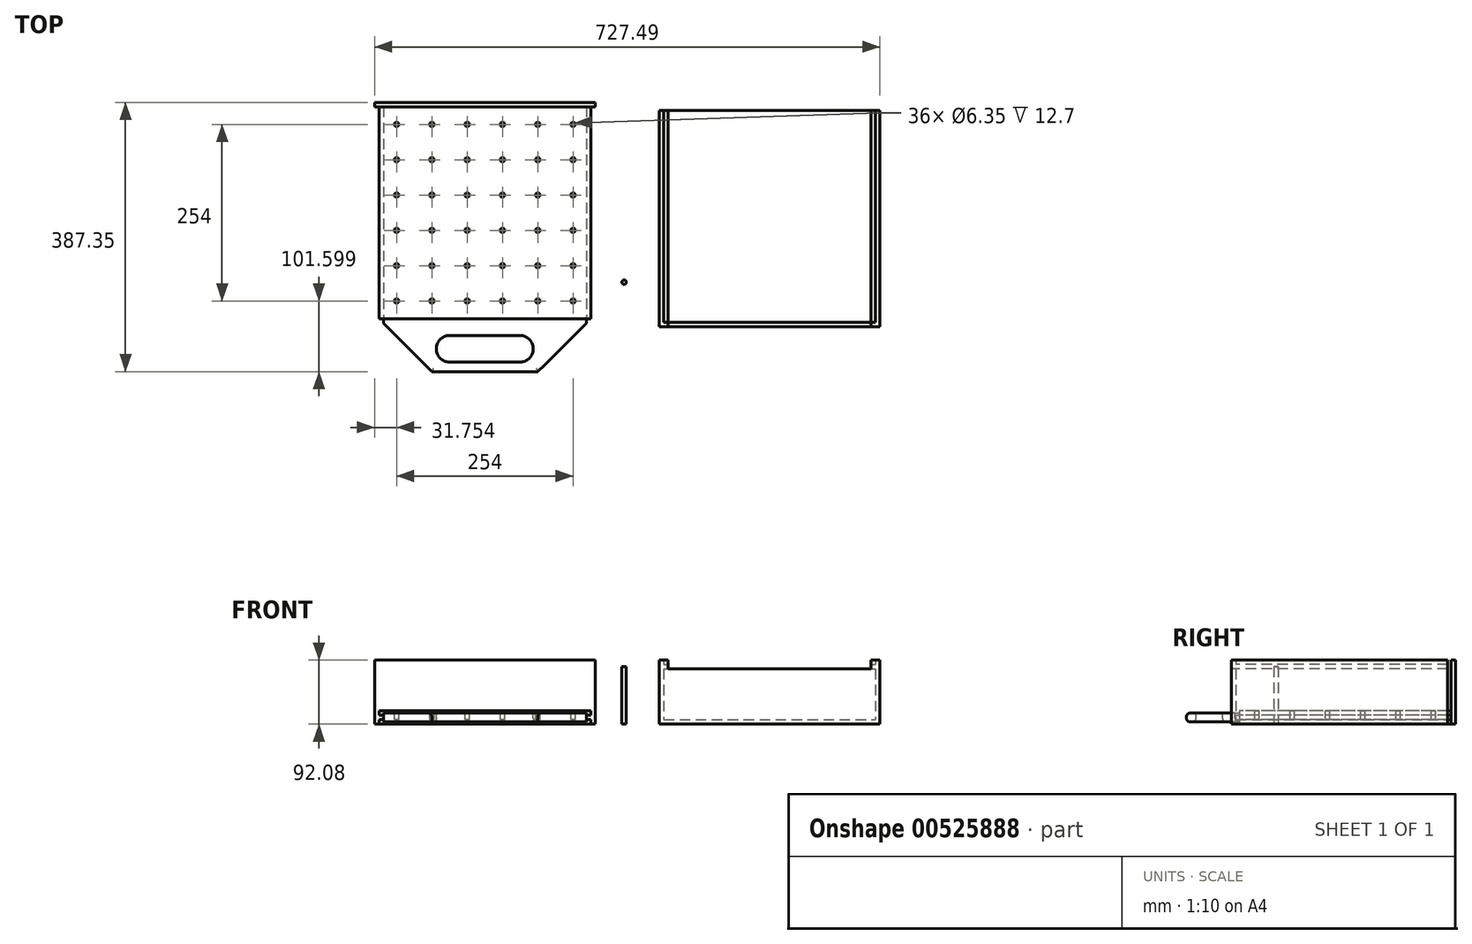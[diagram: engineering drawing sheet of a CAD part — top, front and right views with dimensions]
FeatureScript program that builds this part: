
annotation { "Feature Type Name" : "Feature", "Feature Type Description" : "" }
export const myFeature = defineFeature(function(context is Context, id is Id, definition is map)
    precondition{}
    {
        {
            var Q0;
            Q0=qCreatedBy(makeId("Top.planeOp"),FACE);
            var sketch = newSketch(context, id + "F0", { "sketchPlane" : qUnion([Q0])});
            skLineSegment(sketch, "E0.bottom", {"start": v(-147.49, 152.37) * mm, "end": v(157.31, 152.37) * mm});
            skLineSegment(sketch, "E0.top", {"start": v(-147.49, -152.43) * mm, "end": v(157.31, -152.43) * mm});
            skLineSegment(sketch, "E0.left", {"start": v(-147.49, 152.37) * mm, "end": v(-147.49, -152.43) * mm});
            skLineSegment(sketch, "E0.right", {"start": v(157.31, 152.37) * mm, "end": v(157.31, -152.43) * mm});
            skSolve(sketch);
        }
        {
            var Q0;
            Q0 = qSketchRegion(id + "F0", true);
            extrude(context, id + "F1", {"entities" : qUnion([Q0]), "depth" : 19.05 * mm, "offsetDistance" : 25.4 * mm});
        }
        {
            var Q0;
            Q0=makeQuery(id+"F1.opExtrude","SWEPT_FACE",FACE,{"disambiguationData":[OSD([sQuery(id+"F0.wireOp",EDGE,"E0.top")])]});
            var sketch = newSketch(context, id + "F2", { "sketchPlane" : qUnion([Q0])});
            skLineSegment(sketch, "E1.bottom", {"start": v(-147.49, 12.7) * mm, "end": v(-141.14, 12.7) * mm});
            skLineSegment(sketch, "E1.top", {"start": v(-147.49, 6.35) * mm, "end": v(-141.14, 6.35) * mm});
            skLineSegment(sketch, "E1.left", {"start": v(-147.49, 12.7) * mm, "end": v(-147.49, 6.35) * mm});
            skLineSegment(sketch, "E1.right", {"start": v(-141.14, 12.7) * mm, "end": v(-141.14, 6.35) * mm});
            skLineSegment(sketch, "E2.bottom", {"start": v(150.96, 12.7) * mm, "end": v(157.31, 12.7) * mm});
            skLineSegment(sketch, "E2.top", {"start": v(150.96, 6.35) * mm, "end": v(157.31, 6.35) * mm});
            skLineSegment(sketch, "E2.left", {"start": v(150.96, 12.7) * mm, "end": v(150.96, 6.35) * mm});
            skLineSegment(sketch, "E2.right", {"start": v(157.31, 12.7) * mm, "end": v(157.31, 6.35) * mm});
            skLineSegment(sketch, "E3.bottom", {"start": v(-141.24, 15.88) * mm, "end": v(150.86, 15.88) * mm});
            skLineSegment(sketch, "E3.top", {"start": v(-141.24, 3.18) * mm, "end": v(150.86, 3.18) * mm});
            skLineSegment(sketch, "E3.left", {"start": v(-141.24, 15.88) * mm, "end": v(-141.24, 3.18) * mm});
            skLineSegment(sketch, "E3.right", {"start": v(150.86, 15.88) * mm, "end": v(150.86, 3.18) * mm});
            skSolve(sketch);
        }
        {
            var Q0;
            Q0=makeQuery(id+"F2.imprint","IMPRINT",FACE,{"disambiguationData":[TD([[makeQuery(id+"F2.imprint","IMPRINT",EDGE,{"derivedFrom":sQuery(id+"F2.wireOp",EDGE,"E2.bottom")}),-1.0]])]});
            var Q1;
            {var subQ0=sQuery(id+"F2.wireOp",EDGE,"E1.left");Q1=makeQuery(id+"F2.imprint","IMPRINT",FACE,{"disambiguationData":[TD([[makeQuery(id+"F2.imprint","IMPRINT",EDGE,{"derivedFrom":subQ0}),1.0]])]});}
            extrude(context, id + "F3", {"entities" : qUnion([Q0, Q1]), "operationType" : NewBodyOperationType.REMOVE, "endBound" : BoundingType.THROUGH_ALL, "oppositeDirection" : true, "depth" : 25.4 * mm, "offsetDistance" : 25.4 * mm});
        }
        {
            var Q0;
            {var subQ1=sQuery(id+"F2.wireOp",EDGE,"E1.right");Q0=makeQuery(id+"F2.imprint","IMPRINT",FACE,{"disambiguationData":[TD([[makeQuery(id+"F2.imprint","IMPRINT",EDGE,{"derivedFrom":subQ1}),1.0]])]});}
            extrude(context, id + "F4", {"entities" : qUnion([Q0]), "operationType" : NewBodyOperationType.ADD, "depth" : 76.2 * mm, "offsetDistance" : 25.4 * mm});
        }
        {
            var Q0;
            Q0=makeQuery(id+"F4.opExtrude","SWEPT_FACE",FACE,{"disambiguationData":[OSD([sQuery(id+"F2.wireOp",EDGE,"E3.bottom")])]});
            var sketch = newSketch(context, id + "F5", { "sketchPlane" : qUnion([Q0])});
            skLineSegment(sketch, "E4", {"start": v(-141.24, -158.78) * mm, "end": v(150.86, -158.78) * mm, "construction": true});
            skLineSegment(sketch, "E5", {"start": v(-141.24, -158.78) * mm, "end": v(-71.39, -228.63) * mm});
            skLineSegment(sketch, "E6", {"start": v(150.86, -158.78) * mm, "end": v(81.01, -228.63) * mm});
            skLineSegment(sketch, "E7", {"start": v(-45.99, -195.8) * mm, "end": v(55.61, -195.8) * mm});
            skArc(sketch, "E8.0.startCap", {"start": v(-45.99, -214.85) * mm, "mid": v(-65.04, -195.8) * mm, "end": v(-45.99, -176.75) * mm});
            skArc(sketch, "E8.0.endCap", {"start": v(55.61, -176.75) * mm, "mid": v(74.66, -195.8) * mm, "end": v(55.61, -214.85) * mm});
            skLineSegment(sketch, "E8.0.left", {"start": v(-45.99, -176.75) * mm, "end": v(55.61, -176.75) * mm});
            skLineSegment(sketch, "E8.0.right", {"start": v(-45.99, -214.85) * mm, "end": v(55.61, -214.85) * mm});
            skSolve(sketch);
        }
        {
            var Q0;
            Q0 = qSketchRegion(id + "F5", true);
            var Q1;
            {var subQ0=sQuery(id+"F5.wireOp",EDGE,"E6");Q1=makeQuery(id+"F5.imprint","IMPRINT",FACE,{"disambiguationData":[TD([[makeQuery(id+"F5.imprint","IMPRINT",EDGE,{"derivedFrom":subQ0}),1.0]])]});}
            var Q2;
            {var subQ0=sQuery(id+"F5.wireOp",EDGE,"E5");Q2=makeQuery(id+"F5.imprint","IMPRINT",FACE,{"disambiguationData":[TD([[makeQuery(id+"F5.imprint","IMPRINT",EDGE,{"derivedFrom":subQ0}),-1.0]])]});}
            extrude(context, id + "F6", {"entities" : qUnion([Q0, Q1, Q2]), "operationType" : NewBodyOperationType.REMOVE, "oppositeDirection" : true, "depth" : 25.4 * mm, "offsetDistance" : 25.4 * mm});
        }
        {
            var Q0;
            Q0=makeQuery(id+"F6.boolean.opBoolean","COPY",EDGE,{"derivedFrom":makeQuery(id+"F6.opExtrude","CAP_EDGE",EDGE,{"disambiguationData":[OSD([sQuery(id+"F5.wireOp",EDGE,"E8.0.startCap")])],"isStart":true})});
            var Q1;
            Q1=makeQuery(id+"F6.boolean.opBoolean","COPY",EDGE,{"derivedFrom":makeQuery(id+"F6.opExtrude","CAP_EDGE",EDGE,{"disambiguationData":[OSD([sQuery(id+"F5.wireOp",EDGE,"E8.0.left")])],"isStart":true})});
            var Q2;
            Q2=makeQuery(id+"F6.boolean.opBoolean","INTERSECT",EDGE,{"derivedFrom":[makeQuery(id+"F4.opExtrude","SWEPT_FACE",FACE,{"disambiguationData":[OSD([sQuery(id+"F2.wireOp",EDGE,"E3.top")])]}),makeQuery(id+"F6.opExtrude","SWEPT_FACE",FACE,{"disambiguationData":[OSD([sQuery(id+"F5.wireOp",EDGE,"E8.0.left")])]})]});
            var Q3;
            Q3=makeQuery(id+"F6.boolean.opBoolean","INTERSECT",EDGE,{"derivedFrom":[makeQuery(id+"F4.opExtrude","SWEPT_FACE",FACE,{"disambiguationData":[OSD([sQuery(id+"F2.wireOp",EDGE,"E3.top")])]}),makeQuery(id+"F6.opExtrude","SWEPT_FACE",FACE,{"disambiguationData":[OSD([sQuery(id+"F5.wireOp",EDGE,"E8.0.startCap")])]})]});
            var Q4;
            Q4=makeQuery(id+"F6.boolean.opBoolean","INTERSECT",EDGE,{"derivedFrom":[makeQuery(id+"F4.opExtrude","SWEPT_FACE",FACE,{"disambiguationData":[OSD([sQuery(id+"F2.wireOp",EDGE,"E3.top")])]}),makeQuery(id+"F6.opExtrude","SWEPT_FACE",FACE,{"disambiguationData":[OSD([sQuery(id+"F5.wireOp",EDGE,"E8.0.endCap")])]})]});
            fillet(context, id + "F7", {"entities" : qUnion([Q0, Q1, Q2, Q3, Q4]), "radius" : 5.08 * mm, "tangentPropagation" : true, "allowEdgeOverflow" : false});
        }
        {
            var Q0;
            Q0=makeQuery(id+"F6.boolean.opBoolean","COPY",EDGE,{"derivedFrom":makeQuery(id+"F6.opExtrude","CAP_EDGE",EDGE,{"disambiguationData":[OSD([sQuery(id+"F5.wireOp",EDGE,"E5")])],"isStart":true})});
            var Q1;
            Q1=makeQuery(id+"F6.boolean.opBoolean","INTERSECT",EDGE,{"derivedFrom":[makeQuery(id+"F4.opExtrude","SWEPT_FACE",FACE,{"disambiguationData":[OSD([sQuery(id+"F2.wireOp",EDGE,"E3.top")])]}),makeQuery(id+"F6.opExtrude","SWEPT_FACE",FACE,{"disambiguationData":[OSD([sQuery(id+"F5.wireOp",EDGE,"E5")])]})]});
            var Q2;
            Q2=makeQuery(id+"F4.opExtrude","CAP_EDGE",EDGE,{"disambiguationData":[OSD([sQuery(id+"F2.wireOp",EDGE,"E3.bottom")])],"isStart":false});
            var Q3;
            Q3=makeQuery(id+"F4.opExtrude","CAP_EDGE",EDGE,{"disambiguationData":[OSD([sQuery(id+"F2.wireOp",EDGE,"E3.top")])],"isStart":false});
            var Q4;
            Q4=makeQuery(id+"F6.boolean.opBoolean","INTERSECT",EDGE,{"derivedFrom":[makeQuery(id+"F4.opExtrude","SWEPT_FACE",FACE,{"disambiguationData":[OSD([sQuery(id+"F2.wireOp",EDGE,"E3.top")])]}),makeQuery(id+"F6.opExtrude","SWEPT_FACE",FACE,{"disambiguationData":[OSD([sQuery(id+"F5.wireOp",EDGE,"E6")])]})]});
            var Q5;
            Q5=makeQuery(id+"F6.boolean.opBoolean","COPY",EDGE,{"derivedFrom":makeQuery(id+"F6.opExtrude","CAP_EDGE",EDGE,{"disambiguationData":[OSD([sQuery(id+"F5.wireOp",EDGE,"E6")])],"isStart":true})});
            fillet(context, id + "F8", {"entities" : qUnion([Q0, Q1, Q2, Q3, Q4, Q5]), "radius" : 5.08 * mm, "tangentPropagation" : true, "allowEdgeOverflow" : false});
        }
        {
            var Q0;
            Q0=makeQuery(id+"F1.opExtrude","CAP_FACE",FACE,{"disambiguationData":[OSD([sQuery(id+"F0.wireOp",EDGE,"E0.bottom"),sQuery(id+"F0.wireOp",EDGE,"E0.top"),sQuery(id+"F0.wireOp",EDGE,"E0.left"),sQuery(id+"F0.wireOp",EDGE,"E0.right")])],"isStart":false});
            var sketch = newSketch(context, id + "F9", { "sketchPlane" : qUnion([Q0])});
            skCircle(sketch, "E9", {"center": v(-122.09, -127.03) * mm, "radius": 3.18 * mm});
            skCircle(sketch, "E10.0.1.0", {"center": v(-122.09, -76.23) * mm, "radius": 3.18 * mm});
            skCircle(sketch, "E10.0.2.0", {"center": v(-122.09, -25.43) * mm, "radius": 3.18 * mm});
            skCircle(sketch, "E10.0.3.0", {"center": v(-122.09, 25.37) * mm, "radius": 3.18 * mm});
            skCircle(sketch, "E10.0.4.0", {"center": v(-122.09, 76.17) * mm, "radius": 3.18 * mm});
            skCircle(sketch, "E10.0.5.0", {"center": v(-122.09, 126.97) * mm, "radius": 3.18 * mm});
            skCircle(sketch, "E10.1.0.0", {"center": v(-71.29, -127.03) * mm, "radius": 3.18 * mm});
            skCircle(sketch, "E10.1.1.0", {"center": v(-71.29, -76.23) * mm, "radius": 3.18 * mm});
            skCircle(sketch, "E10.1.2.0", {"center": v(-71.29, -25.43) * mm, "radius": 3.18 * mm});
            skCircle(sketch, "E10.1.3.0", {"center": v(-71.29, 25.37) * mm, "radius": 3.18 * mm});
            skCircle(sketch, "E10.1.4.0", {"center": v(-71.29, 76.17) * mm, "radius": 3.18 * mm});
            skCircle(sketch, "E10.1.5.0", {"center": v(-71.29, 126.97) * mm, "radius": 3.18 * mm});
            skCircle(sketch, "E10.2.0.0", {"center": v(-20.49, -127.03) * mm, "radius": 3.18 * mm});
            skCircle(sketch, "E10.2.1.0", {"center": v(-20.49, -76.23) * mm, "radius": 3.18 * mm});
            skCircle(sketch, "E10.2.2.0", {"center": v(-20.49, -25.43) * mm, "radius": 3.18 * mm});
            skCircle(sketch, "E10.2.3.0", {"center": v(-20.49, 25.37) * mm, "radius": 3.18 * mm});
            skCircle(sketch, "E10.2.4.0", {"center": v(-20.49, 76.17) * mm, "radius": 3.18 * mm});
            skCircle(sketch, "E10.2.5.0", {"center": v(-20.49, 126.97) * mm, "radius": 3.18 * mm});
            skCircle(sketch, "E10.3.0.0", {"center": v(30.31, -127.03) * mm, "radius": 3.18 * mm});
            skCircle(sketch, "E10.3.1.0", {"center": v(30.31, -76.23) * mm, "radius": 3.18 * mm});
            skCircle(sketch, "E10.3.2.0", {"center": v(30.31, -25.43) * mm, "radius": 3.18 * mm});
            skCircle(sketch, "E10.3.3.0", {"center": v(30.31, 25.37) * mm, "radius": 3.18 * mm});
            skCircle(sketch, "E10.3.4.0", {"center": v(30.31, 76.17) * mm, "radius": 3.18 * mm});
            skCircle(sketch, "E10.3.5.0", {"center": v(30.31, 126.97) * mm, "radius": 3.18 * mm});
            skCircle(sketch, "E10.4.0.0", {"center": v(81.11, -127.03) * mm, "radius": 3.18 * mm});
            skCircle(sketch, "E10.4.1.0", {"center": v(81.11, -76.23) * mm, "radius": 3.18 * mm});
            skCircle(sketch, "E10.4.2.0", {"center": v(81.11, -25.43) * mm, "radius": 3.18 * mm});
            skCircle(sketch, "E10.4.3.0", {"center": v(81.11, 25.37) * mm, "radius": 3.18 * mm});
            skCircle(sketch, "E10.4.4.0", {"center": v(81.11, 76.17) * mm, "radius": 3.18 * mm});
            skCircle(sketch, "E10.4.5.0", {"center": v(81.11, 126.97) * mm, "radius": 3.18 * mm});
            skCircle(sketch, "E10.5.0.0", {"center": v(131.91, -127.03) * mm, "radius": 3.18 * mm});
            skCircle(sketch, "E10.5.1.0", {"center": v(131.91, -76.23) * mm, "radius": 3.18 * mm});
            skCircle(sketch, "E10.5.2.0", {"center": v(131.91, -25.43) * mm, "radius": 3.18 * mm});
            skCircle(sketch, "E10.5.3.0", {"center": v(131.91, 25.37) * mm, "radius": 3.18 * mm});
            skCircle(sketch, "E10.5.4.0", {"center": v(131.91, 76.17) * mm, "radius": 3.18 * mm});
            skCircle(sketch, "E10.5.5.0", {"center": v(131.91, 126.97) * mm, "radius": 3.18 * mm});
            skLineSegment(sketch, "E10.direction1", {"start": v(-122.09, -127.03) * mm, "end": v(-71.29, -127.03) * mm, "construction": true});
            skLineSegment(sketch, "E10.direction2", {"start": v(-122.09, -127.03) * mm, "end": v(-122.09, -76.23) * mm, "construction": true});
            skSolve(sketch);
        }
        {
            var Q0;
            Q0=makeQuery(id+"F9.imprint","IMPRINT",FACE,{"disambiguationData":[TD([[makeQuery(id+"F9.imprint","IMPRINT",EDGE,{"derivedFrom":sQuery(id+"F9.wireOp",EDGE,"E10.5.4.0")}),1.0]])]});
            var Q1;
            Q1=makeQuery(id+"F9.imprint","IMPRINT",FACE,{"disambiguationData":[TD([[makeQuery(id+"F9.imprint","IMPRINT",EDGE,{"derivedFrom":sQuery(id+"F9.wireOp",EDGE,"E10.3.0.0")}),1.0]])]});
            var Q2;
            Q2=makeQuery(id+"F9.imprint","IMPRINT",FACE,{"disambiguationData":[TD([[makeQuery(id+"F9.imprint","IMPRINT",EDGE,{"derivedFrom":sQuery(id+"F9.wireOp",EDGE,"E10.5.1.0")}),1.0]])]});
            var Q3;
            Q3=makeQuery(id+"F9.imprint","IMPRINT",FACE,{"disambiguationData":[TD([[makeQuery(id+"F9.imprint","IMPRINT",EDGE,{"derivedFrom":sQuery(id+"F9.wireOp",EDGE,"E10.4.1.0")}),1.0]])]});
            var Q4;
            Q4=makeQuery(id+"F9.imprint","IMPRINT",FACE,{"disambiguationData":[TD([[makeQuery(id+"F9.imprint","IMPRINT",EDGE,{"derivedFrom":sQuery(id+"F9.wireOp",EDGE,"E10.5.5.0")}),1.0]])]});
            var Q5;
            Q5=makeQuery(id+"F9.imprint","IMPRINT",FACE,{"disambiguationData":[TD([[makeQuery(id+"F9.imprint","IMPRINT",EDGE,{"derivedFrom":sQuery(id+"F9.wireOp",EDGE,"E10.3.1.0")}),1.0]])]});
            var Q6;
            Q6=makeQuery(id+"F9.imprint","IMPRINT",FACE,{"disambiguationData":[TD([[makeQuery(id+"F9.imprint","IMPRINT",EDGE,{"derivedFrom":sQuery(id+"F9.wireOp",EDGE,"E10.2.3.0")}),1.0]])]});
            var Q7;
            Q7=makeQuery(id+"F9.imprint","IMPRINT",FACE,{"disambiguationData":[TD([[makeQuery(id+"F9.imprint","IMPRINT",EDGE,{"derivedFrom":sQuery(id+"F9.wireOp",EDGE,"E10.2.1.0")}),1.0]])]});
            var Q8;
            Q8=makeQuery(id+"F9.imprint","IMPRINT",FACE,{"disambiguationData":[TD([[makeQuery(id+"F9.imprint","IMPRINT",EDGE,{"derivedFrom":sQuery(id+"F9.wireOp",EDGE,"E10.2.2.0")}),1.0]])]});
            var Q9;
            Q9=makeQuery(id+"F9.imprint","IMPRINT",FACE,{"disambiguationData":[TD([[makeQuery(id+"F9.imprint","IMPRINT",EDGE,{"derivedFrom":sQuery(id+"F9.wireOp",EDGE,"E9")}),1.0]])]});
            var Q10;
            Q10=makeQuery(id+"F9.imprint","IMPRINT",FACE,{"disambiguationData":[TD([[makeQuery(id+"F9.imprint","IMPRINT",EDGE,{"derivedFrom":sQuery(id+"F9.wireOp",EDGE,"E10.0.1.0")}),1.0]])]});
            var Q11;
            Q11=makeQuery(id+"F9.imprint","IMPRINT",FACE,{"disambiguationData":[TD([[makeQuery(id+"F9.imprint","IMPRINT",EDGE,{"derivedFrom":sQuery(id+"F9.wireOp",EDGE,"E10.0.2.0")}),1.0]])]});
            var Q12;
            Q12=makeQuery(id+"F9.imprint","IMPRINT",FACE,{"disambiguationData":[TD([[makeQuery(id+"F9.imprint","IMPRINT",EDGE,{"derivedFrom":sQuery(id+"F9.wireOp",EDGE,"E10.0.3.0")}),1.0]])]});
            var Q13;
            Q13=makeQuery(id+"F9.imprint","IMPRINT",FACE,{"disambiguationData":[TD([[makeQuery(id+"F9.imprint","IMPRINT",EDGE,{"derivedFrom":sQuery(id+"F9.wireOp",EDGE,"E10.0.4.0")}),1.0]])]});
            var Q14;
            Q14=makeQuery(id+"F9.imprint","IMPRINT",FACE,{"disambiguationData":[TD([[makeQuery(id+"F9.imprint","IMPRINT",EDGE,{"derivedFrom":sQuery(id+"F9.wireOp",EDGE,"E10.0.5.0")}),1.0]])]});
            var Q15;
            Q15=makeQuery(id+"F9.imprint","IMPRINT",FACE,{"disambiguationData":[TD([[makeQuery(id+"F9.imprint","IMPRINT",EDGE,{"derivedFrom":sQuery(id+"F9.wireOp",EDGE,"E10.3.4.0")}),1.0]])]});
            var Q16;
            Q16=makeQuery(id+"F9.imprint","IMPRINT",FACE,{"disambiguationData":[TD([[makeQuery(id+"F9.imprint","IMPRINT",EDGE,{"derivedFrom":sQuery(id+"F9.wireOp",EDGE,"E10.1.0.0")}),1.0]])]});
            var Q17;
            Q17=makeQuery(id+"F9.imprint","IMPRINT",FACE,{"disambiguationData":[TD([[makeQuery(id+"F9.imprint","IMPRINT",EDGE,{"derivedFrom":sQuery(id+"F9.wireOp",EDGE,"E10.1.1.0")}),1.0]])]});
            var Q18;
            Q18=makeQuery(id+"F9.imprint","IMPRINT",FACE,{"disambiguationData":[TD([[makeQuery(id+"F9.imprint","IMPRINT",EDGE,{"derivedFrom":sQuery(id+"F9.wireOp",EDGE,"E10.1.2.0")}),1.0]])]});
            var Q19;
            Q19=makeQuery(id+"F9.imprint","IMPRINT",FACE,{"disambiguationData":[TD([[makeQuery(id+"F9.imprint","IMPRINT",EDGE,{"derivedFrom":sQuery(id+"F9.wireOp",EDGE,"E10.1.3.0")}),1.0]])]});
            var Q20;
            Q20=makeQuery(id+"F9.imprint","IMPRINT",FACE,{"disambiguationData":[TD([[makeQuery(id+"F9.imprint","IMPRINT",EDGE,{"derivedFrom":sQuery(id+"F9.wireOp",EDGE,"E10.1.4.0")}),1.0]])]});
            var Q21;
            Q21=makeQuery(id+"F9.imprint","IMPRINT",FACE,{"disambiguationData":[TD([[makeQuery(id+"F9.imprint","IMPRINT",EDGE,{"derivedFrom":sQuery(id+"F9.wireOp",EDGE,"E10.1.5.0")}),1.0]])]});
            var Q22;
            Q22=makeQuery(id+"F9.imprint","IMPRINT",FACE,{"disambiguationData":[TD([[makeQuery(id+"F9.imprint","IMPRINT",EDGE,{"derivedFrom":sQuery(id+"F9.wireOp",EDGE,"E10.2.0.0")}),1.0]])]});
            var Q23;
            Q23=makeQuery(id+"F9.imprint","IMPRINT",FACE,{"disambiguationData":[TD([[makeQuery(id+"F9.imprint","IMPRINT",EDGE,{"derivedFrom":sQuery(id+"F9.wireOp",EDGE,"E10.4.2.0")}),1.0]])]});
            var Q24;
            Q24=makeQuery(id+"F9.imprint","IMPRINT",FACE,{"disambiguationData":[TD([[makeQuery(id+"F9.imprint","IMPRINT",EDGE,{"derivedFrom":sQuery(id+"F9.wireOp",EDGE,"E10.4.5.0")}),1.0]])]});
            var Q25;
            Q25=makeQuery(id+"F9.imprint","IMPRINT",FACE,{"disambiguationData":[TD([[makeQuery(id+"F9.imprint","IMPRINT",EDGE,{"derivedFrom":sQuery(id+"F9.wireOp",EDGE,"E10.3.2.0")}),1.0]])]});
            var Q26;
            Q26=makeQuery(id+"F9.imprint","IMPRINT",FACE,{"disambiguationData":[TD([[makeQuery(id+"F9.imprint","IMPRINT",EDGE,{"derivedFrom":sQuery(id+"F9.wireOp",EDGE,"E10.3.5.0")}),1.0]])]});
            var Q27;
            Q27=makeQuery(id+"F9.imprint","IMPRINT",FACE,{"disambiguationData":[TD([[makeQuery(id+"F9.imprint","IMPRINT",EDGE,{"derivedFrom":sQuery(id+"F9.wireOp",EDGE,"E10.5.2.0")}),1.0]])]});
            var Q28;
            Q28=makeQuery(id+"F9.imprint","IMPRINT",FACE,{"disambiguationData":[TD([[makeQuery(id+"F9.imprint","IMPRINT",EDGE,{"derivedFrom":sQuery(id+"F9.wireOp",EDGE,"E10.2.4.0")}),1.0]])]});
            var Q29;
            Q29=makeQuery(id+"F9.imprint","IMPRINT",FACE,{"disambiguationData":[TD([[makeQuery(id+"F9.imprint","IMPRINT",EDGE,{"derivedFrom":sQuery(id+"F9.wireOp",EDGE,"E10.4.3.0")}),1.0]])]});
            var Q30;
            Q30=makeQuery(id+"F9.imprint","IMPRINT",FACE,{"disambiguationData":[TD([[makeQuery(id+"F9.imprint","IMPRINT",EDGE,{"derivedFrom":sQuery(id+"F9.wireOp",EDGE,"E10.5.0.0")}),1.0]])]});
            var Q31;
            Q31=makeQuery(id+"F9.imprint","IMPRINT",FACE,{"disambiguationData":[TD([[makeQuery(id+"F9.imprint","IMPRINT",EDGE,{"derivedFrom":sQuery(id+"F9.wireOp",EDGE,"E10.3.3.0")}),1.0]])]});
            var Q32;
            Q32=makeQuery(id+"F9.imprint","IMPRINT",FACE,{"disambiguationData":[TD([[makeQuery(id+"F9.imprint","IMPRINT",EDGE,{"derivedFrom":sQuery(id+"F9.wireOp",EDGE,"E10.4.0.0")}),1.0]])]});
            var Q33;
            Q33=makeQuery(id+"F9.imprint","IMPRINT",FACE,{"disambiguationData":[TD([[makeQuery(id+"F9.imprint","IMPRINT",EDGE,{"derivedFrom":sQuery(id+"F9.wireOp",EDGE,"E10.5.3.0")}),1.0]])]});
            var Q34;
            Q34=makeQuery(id+"F9.imprint","IMPRINT",FACE,{"disambiguationData":[TD([[makeQuery(id+"F9.imprint","IMPRINT",EDGE,{"derivedFrom":sQuery(id+"F9.wireOp",EDGE,"E10.2.5.0")}),1.0]])]});
            var Q35;
            Q35=makeQuery(id+"F9.imprint","IMPRINT",FACE,{"disambiguationData":[TD([[makeQuery(id+"F9.imprint","IMPRINT",EDGE,{"derivedFrom":sQuery(id+"F9.wireOp",EDGE,"E10.4.4.0")}),1.0]])]});
            extrude(context, id + "F10", {"entities" : qUnion([Q0, Q1, Q2, Q3, Q4, Q5, Q6, Q7, Q8, Q9, Q10, Q11, Q12, Q13, Q14, Q15, Q16, Q17, Q18, Q19, Q20, Q21, Q22, Q23, Q24, Q25, Q26, Q27, Q28, Q29, Q30, Q31, Q32, Q33, Q34, Q35]), "operationType" : NewBodyOperationType.REMOVE, "oppositeDirection" : true, "depth" : 12.7 * mm, "offsetDistance" : 25.4 * mm});
        }
        {
            var Q0;
            Q0=qCreatedBy(makeId("Top.planeOp"),FACE);
            var sketch = newSketch(context, id + "F11", { "sketchPlane" : qUnion([Q0])});
            skCircle(sketch, "E11", {"center": v(205.43, -99.97) * mm, "radius": 3.18 * mm});
            skSolve(sketch);
        }
        {
            var Q0;
            Q0 = qSketchRegion(id + "F11", true);
            extrude(context, id + "F12", {"entities" : qUnion([Q0]), "depth" : 82.55 * mm, "offsetDistance" : 25.4 * mm});
        }
        {
            var Q0;
            Q0=makeQuery(id+"F1.opExtrude","SWEPT_FACE",FACE,{"disambiguationData":[OSD([sQuery(id+"F0.wireOp",EDGE,"E0.bottom")])]});
            var sketch = newSketch(context, id + "F13", { "sketchPlane" : qUnion([Q0])});
            skLineSegment(sketch, "E12.bottom", {"start": v(-157.31, 0) * mm, "end": v(147.49, 0) * mm});
            skLineSegment(sketch, "E12.top", {"start": v(-157.31, 92.08) * mm, "end": v(147.49, 92.08) * mm});
            skLineSegment(sketch, "E12.left", {"start": v(-157.31, 0) * mm, "end": v(-157.31, 92.08) * mm});
            skLineSegment(sketch, "E12.right", {"start": v(147.49, 0) * mm, "end": v(147.49, 92.08) * mm});
            skLineSegment(sketch, "E13", {"start": v(0, 0) * mm, "end": v(0, 92.08) * mm, "construction": true});
            skSolve(sketch);
        }
        {
            var Q0;
            {var subQ0=sQuery(id+"F13.wireOp",EDGE,"E12.top");Q0=makeQuery(id+"F13.imprint","IMPRINT",FACE,{"disambiguationData":[TD([[makeQuery(id+"F13.imprint","IMPRINT",EDGE,{"derivedFrom":subQ0}),-1.0]])]});}
            var Q1;
            {var subQ7=sQuery(id+"F13.wireOp",EDGE,"E12.bottom");Q1=makeQuery(id+"F13.imprint","IMPRINT",FACE,{"disambiguationData":[TD([[makeQuery(id+"F13.imprint","IMPRINT",EDGE,{"derivedFrom":subQ7}),-1.0]])]});}
            var Q2;
            {var subQ1=makeQuery(id+"F1.opExtrude","SWEPT_FACE",FACE,{"disambiguationData":[OSD([sQuery(id+"F0.wireOp",EDGE,"E0.bottom")])]});var subQ2=makeQuery(id+"F3.boolean.opBoolean","INTERSECT",EDGE,{"derivedFrom":[subQ1,makeQuery(id+"F3.opExtrude","SWEPT_FACE",FACE,{"disambiguationData":[OSD([sQuery(id+"F2.wireOp",EDGE,"E2.bottom")])]})]});Q2=makeQuery(id+"F13.imprint","IMPRINT",FACE,{"disambiguationData":[TD([[makeQuery(id+"F13.imprint","IMPRINT",EDGE,{"derivedFrom":subQ2}),-1.0]])]});}
            var Q3;
            {var subQ1=makeQuery(id+"F1.opExtrude","SWEPT_FACE",FACE,{"disambiguationData":[OSD([sQuery(id+"F0.wireOp",EDGE,"E0.bottom")])]});var subQ2=makeQuery(id+"F3.boolean.opBoolean","INTERSECT",EDGE,{"derivedFrom":[subQ1,makeQuery(id+"F3.opExtrude","SWEPT_FACE",FACE,{"disambiguationData":[OSD([sQuery(id+"F2.wireOp",EDGE,"E1.bottom")])]})]});Q3=makeQuery(id+"F13.imprint","IMPRINT",FACE,{"disambiguationData":[TD([[makeQuery(id+"F13.imprint","IMPRINT",EDGE,{"derivedFrom":subQ2}),-1.0]])]});}
            extrude(context, id + "F14", {"entities" : qUnion([Q0, Q1, Q2, Q3]), "operationType" : NewBodyOperationType.ADD, "depth" : 6.35 * mm, "offsetDistance" : 25.4 * mm});
        }
        {
            var Q0;
            {var subQ2=sQuery(id+"F0.wireOp",EDGE,"E0.right");var subQ6=makeQuery(id+"F1.opExtrude","SWEPT_FACE",FACE,{"disambiguationData":[OSD([subQ2])]});Q0=makeQuery(id+"F14.boolean.opBoolean","MERGE",FACE,{"derivedFrom":[makeQuery(id+"F3.boolean.opBoolean","SPLIT",FACE,{"disambiguationData":[TD([makeQuery(id+"F3.opExtrude","SWEPT_FACE",FACE,{"disambiguationData":[OSD([sQuery(id+"F2.wireOp",EDGE,"E2.top")])]})])],"derivedFrom":subQ6}),makeQuery(id+"F3.boolean.opBoolean","SPLIT",FACE,{"disambiguationData":[TD([makeQuery(id+"F3.opExtrude","SWEPT_FACE",FACE,{"disambiguationData":[OSD([sQuery(id+"F2.wireOp",EDGE,"E2.bottom")])]})])],"derivedFrom":subQ6}),makeQuery(id+"F14.opExtrude","SWEPT_FACE",FACE,{"disambiguationData":[OSD([sQuery(id+"F13.wireOp",EDGE,"E12.left")])]})]});}
            var sketch = newSketch(context, id + "F15", { "sketchPlane" : qUnion([Q0])});
            skLineSegment(sketch, "E14", {"start": v(152.37, 19.05) * mm, "end": v(152.37, 0) * mm});
            skSolve(sketch);
        }
        {
            var Q0;
            {var subQ0=sQuery(id+"F13.wireOp",EDGE,"E12.left");var subQ12=makeQuery(id+"F14.opExtrude","CAP_EDGE",EDGE,{"disambiguationData":[OSD([subQ0])],"isStart":false});Q0=makeQuery(id+"F15.imprint","IMPRINT",FACE,{"disambiguationData":[TD([[makeQuery(id+"F15.imprint","IMPRINT",EDGE,{"derivedFrom":subQ12}),1.0]])]});}
            extrude(context, id + "F16", {"entities" : qUnion([Q0]), "operationType" : NewBodyOperationType.ADD, "depth" : 6.35 * mm, "offsetDistance" : 25.4 * mm});
        }
        {
            var Q0;
            {var subQ3=sQuery(id+"F0.wireOp",EDGE,"E0.left");var subQ6=makeQuery(id+"F1.opExtrude","SWEPT_FACE",FACE,{"disambiguationData":[OSD([subQ3])]});Q0=makeQuery(id+"F14.boolean.opBoolean","MERGE",FACE,{"derivedFrom":[makeQuery(id+"F3.boolean.opBoolean","SPLIT",FACE,{"disambiguationData":[TD([makeQuery(id+"F3.opExtrude","SWEPT_FACE",FACE,{"disambiguationData":[OSD([sQuery(id+"F2.wireOp",EDGE,"E1.top")])]})])],"derivedFrom":subQ6}),makeQuery(id+"F3.boolean.opBoolean","SPLIT",FACE,{"disambiguationData":[TD([makeQuery(id+"F3.opExtrude","SWEPT_FACE",FACE,{"disambiguationData":[OSD([sQuery(id+"F2.wireOp",EDGE,"E1.bottom")])]})])],"derivedFrom":subQ6}),makeQuery(id+"F14.opExtrude","SWEPT_FACE",FACE,{"disambiguationData":[OSD([sQuery(id+"F13.wireOp",EDGE,"E12.right")])]})]});}
            var sketch = newSketch(context, id + "F17", { "sketchPlane" : qUnion([Q0])});
            skLineSegment(sketch, "E15", {"start": v(-152.37, 19.05) * mm, "end": v(-152.37, 0) * mm});
            skSolve(sketch);
        }
        {
            var Q0;
            {var subQ0=sQuery(id+"F13.wireOp",EDGE,"E12.right");var subQ12=makeQuery(id+"F14.opExtrude","CAP_EDGE",EDGE,{"disambiguationData":[OSD([subQ0])],"isStart":false});Q0=makeQuery(id+"F17.imprint","IMPRINT",FACE,{"disambiguationData":[TD([[makeQuery(id+"F17.imprint","IMPRINT",EDGE,{"derivedFrom":subQ12}),-1.0]])]});}
            extrude(context, id + "F18", {"entities" : qUnion([Q0]), "operationType" : NewBodyOperationType.ADD, "depth" : 6.35 * mm, "offsetDistance" : 25.4 * mm});
        }
        {
            var Q0;
            Q0=qCreatedBy(makeId("Top.planeOp"),FACE);
            var sketch = newSketch(context, id + "F19", { "sketchPlane" : qUnion([Q0])});
            skLineSegment(sketch, "E16.bottom", {"start": v(256.15, -163.77) * mm, "end": v(573.65, -163.77) * mm});
            skLineSegment(sketch, "E16.top", {"start": v(256.15, 153.73) * mm, "end": v(573.65, 153.73) * mm});
            skLineSegment(sketch, "E16.left", {"start": v(256.15, -163.77) * mm, "end": v(256.15, 153.73) * mm});
            skLineSegment(sketch, "E16.right", {"start": v(573.65, -163.77) * mm, "end": v(573.65, 153.73) * mm});
            skSolve(sketch);
        }
        {
            var Q0;
            Q0=makeQuery(id+"F19.imprint","IMPRINT",FACE,{"disambiguationData":[TD([[makeQuery(id+"F19.imprint","IMPRINT",EDGE,{"derivedFrom":sQuery(id+"F19.wireOp",EDGE,"E16.bottom")}),1.0]])]});
            extrude(context, id + "F20", {"entities" : qUnion([Q0]), "depth" : 92.07 * mm, "offsetDistance" : 25.4 * mm});
        }
        {
            var Q0;
            Q0=makeQuery(id+"F20.opExtrude","CAP_FACE",FACE,{"disambiguationData":[OSD([sQuery(id+"F19.wireOp",EDGE,"E16.bottom"),sQuery(id+"F19.wireOp",EDGE,"E16.top"),sQuery(id+"F19.wireOp",EDGE,"E16.left"),sQuery(id+"F19.wireOp",EDGE,"E16.right")])],"isStart":false});
            shell(context, id + "F21", {"entities" : qUnion([Q0]), "thickness" : 6.35 * mm});
        }
        {
            var Q0;
            Q0=makeQuery(id+"F20.opExtrude","CAP_FACE",FACE,{"disambiguationData":[OSD([sQuery(id+"F19.wireOp",EDGE,"E16.bottom"),sQuery(id+"F19.wireOp",EDGE,"E16.top"),sQuery(id+"F19.wireOp",EDGE,"E16.left"),sQuery(id+"F19.wireOp",EDGE,"E16.right")])],"isStart":false});
            var sketch = newSketch(context, id + "F22", { "sketchPlane" : qUnion([Q0])});
            skLineSegment(sketch, "E17", {"start": v(262.5, 147.38) * mm, "end": v(256.15, 147.38) * mm});
            skLineSegment(sketch, "E18", {"start": v(567.3, 147.38) * mm, "end": v(573.65, 147.38) * mm});
            skLineSegment(sketch, "E19", {"start": v(262.5, -157.42) * mm, "end": v(262.5, -163.77) * mm});
            skLineSegment(sketch, "E20", {"start": v(567.3, -157.42) * mm, "end": v(567.3, -163.77) * mm});
            skSolve(sketch);
        }
        {
            var Q0;
            {var subQ4=sQuery(id+"F22.wireOp",EDGE,"E17");Q0=makeQuery(id+"F22.imprint","IMPRINT",FACE,{"disambiguationData":[TD([[makeQuery(id+"F22.imprint","IMPRINT",EDGE,{"derivedFrom":subQ4}),-1.0]])]});}
            extrude(context, id + "F23", {"entities" : qUnion([Q0]), "operationType" : NewBodyOperationType.REMOVE, "endBound" : BoundingType.THROUGH_ALL, "oppositeDirection" : true, "depth" : 25.4 * mm, "offsetDistance" : 25.4 * mm});
        }
        {
            var Q0;
            {var subQ0=sQuery(id+"F22.wireOp",EDGE,"E19");Q0=makeQuery(id+"F22.imprint","IMPRINT",FACE,{"disambiguationData":[TD([[makeQuery(id+"F22.imprint","IMPRINT",EDGE,{"derivedFrom":subQ0}),1.0]])]});}
            extrude(context, id + "F24", {"entities" : qUnion([Q0]), "operationType" : NewBodyOperationType.REMOVE, "oppositeDirection" : true, "depth" : 12.7 * mm, "offsetDistance" : 25.4 * mm});
        }
        {
            var Q0;
            Q0=makeQuery(id+"F24.boolean.opBoolean","MERGE",FACE,{"derivedFrom":[makeQuery(id+"F21.opShell","OFFSET_FACE",FACE,{"disambiguationData":[OSD([sQuery(id+"F19.wireOp",EDGE,"E16.left")])]}),makeQuery(id+"F24.opExtrude","SWEPT_FACE",FACE,{"disambiguationData":[OSD([sQuery(id+"F22.wireOp",EDGE,"E19")])]})]});
            var sketch = newSketch(context, id + "F25", { "sketchPlane" : qUnion([Q0])});
            skLineSegment(sketch, "E21.bottom", {"start": v(-163.77, 85.73) * mm, "end": v(147.38, 85.73) * mm});
            skLineSegment(sketch, "E21.top", {"start": v(-163.77, 79.38) * mm, "end": v(147.38, 79.38) * mm});
            skLineSegment(sketch, "E21.left", {"start": v(-163.77, 85.73) * mm, "end": v(-163.77, 79.38) * mm});
            skLineSegment(sketch, "E21.right", {"start": v(147.38, 85.73) * mm, "end": v(147.38, 79.38) * mm});
            skSolve(sketch);
        }
        {
            var Q0;
            Q0=makeQuery(id+"F25.imprint","IMPRINT",FACE,{"disambiguationData":[TD([[makeQuery(id+"F25.imprint","IMPRINT",EDGE,{"derivedFrom":sQuery(id+"F25.wireOp",EDGE,"E21.bottom")}),-1.0]])]});
            extrude(context, id + "F26", {"entities" : qUnion([Q0]), "operationType" : NewBodyOperationType.ADD, "depth" : 6.35 * mm, "offsetDistance" : 25.4 * mm});
        }
        {
            var Q0;
            Q0=makeQuery(id+"F24.boolean.opBoolean","MERGE",FACE,{"derivedFrom":[makeQuery(id+"F21.opShell","OFFSET_FACE",FACE,{"disambiguationData":[OSD([sQuery(id+"F19.wireOp",EDGE,"E16.right")])]}),makeQuery(id+"F24.opExtrude","SWEPT_FACE",FACE,{"disambiguationData":[OSD([sQuery(id+"F22.wireOp",EDGE,"E20")])]})]});
            var sketch = newSketch(context, id + "F27", { "sketchPlane" : qUnion([Q0])});
            skLineSegment(sketch, "E22.bottom", {"start": v(-147.38, 85.73) * mm, "end": v(163.77, 85.73) * mm});
            skLineSegment(sketch, "E22.top", {"start": v(-147.38, 79.38) * mm, "end": v(163.77, 79.38) * mm});
            skLineSegment(sketch, "E22.left", {"start": v(-147.38, 85.73) * mm, "end": v(-147.38, 79.38) * mm});
            skLineSegment(sketch, "E22.right", {"start": v(163.77, 85.73) * mm, "end": v(163.77, 79.38) * mm});
            skSolve(sketch);
        }
        {
            var Q0;
            Q0=makeQuery(id+"F27.imprint","IMPRINT",FACE,{"disambiguationData":[TD([[makeQuery(id+"F27.imprint","IMPRINT",EDGE,{"derivedFrom":sQuery(id+"F27.wireOp",EDGE,"E22.bottom")}),-1.0]])]});
            extrude(context, id + "F28", {"entities" : qUnion([Q0]), "operationType" : NewBodyOperationType.ADD, "depth" : 6.35 * mm, "offsetDistance" : 25.4 * mm});
        }
        {
            var Q0;
            Q0=makeQuery(id+"F26.opExtrude","SWEPT_FACE",FACE,{"disambiguationData":[OSD([sQuery(id+"F25.wireOp",EDGE,"E21.bottom")])]});
            var sketch = newSketch(context, id + "F29", { "sketchPlane" : qUnion([Q0])});
            skLineSegment(sketch, "E23", {"start": v(262.5, -157.42) * mm, "end": v(268.85, -157.42) * mm});
            skSolve(sketch);
        }
        {
            var Q0;
            {var subQ0=sQuery(id+"F29.wireOp",EDGE,"E23");Q0=makeQuery(id+"F29.imprint","IMPRINT",FACE,{"disambiguationData":[TD([[makeQuery(id+"F29.imprint","IMPRINT",EDGE,{"derivedFrom":subQ0}),-1.0]])]});}
            extrude(context, id + "F30", {"entities" : qUnion([Q0]), "operationType" : NewBodyOperationType.ADD, "depth" : 6.35 * mm, "offsetDistance" : 25.4 * mm});
        }
        {
            var Q0;
            Q0=makeQuery(id+"F28.opExtrude","SWEPT_FACE",FACE,{"disambiguationData":[OSD([sQuery(id+"F27.wireOp",EDGE,"E22.bottom")])]});
            var sketch = newSketch(context, id + "F31", { "sketchPlane" : qUnion([Q0])});
            skLineSegment(sketch, "E24", {"start": v(560.95, -157.42) * mm, "end": v(567.3, -157.42) * mm});
            skSolve(sketch);
        }
        {
            var Q0;
            {var subQ0=sQuery(id+"F31.wireOp",EDGE,"E24");Q0=makeQuery(id+"F31.imprint","IMPRINT",FACE,{"disambiguationData":[TD([[makeQuery(id+"F31.imprint","IMPRINT",EDGE,{"derivedFrom":subQ0}),-1.0]])]});}
            extrude(context, id + "F32", {"entities" : qUnion([Q0]), "operationType" : NewBodyOperationType.ADD, "depth" : 6.35 * mm, "offsetDistance" : 25.4 * mm});
        }
    });
